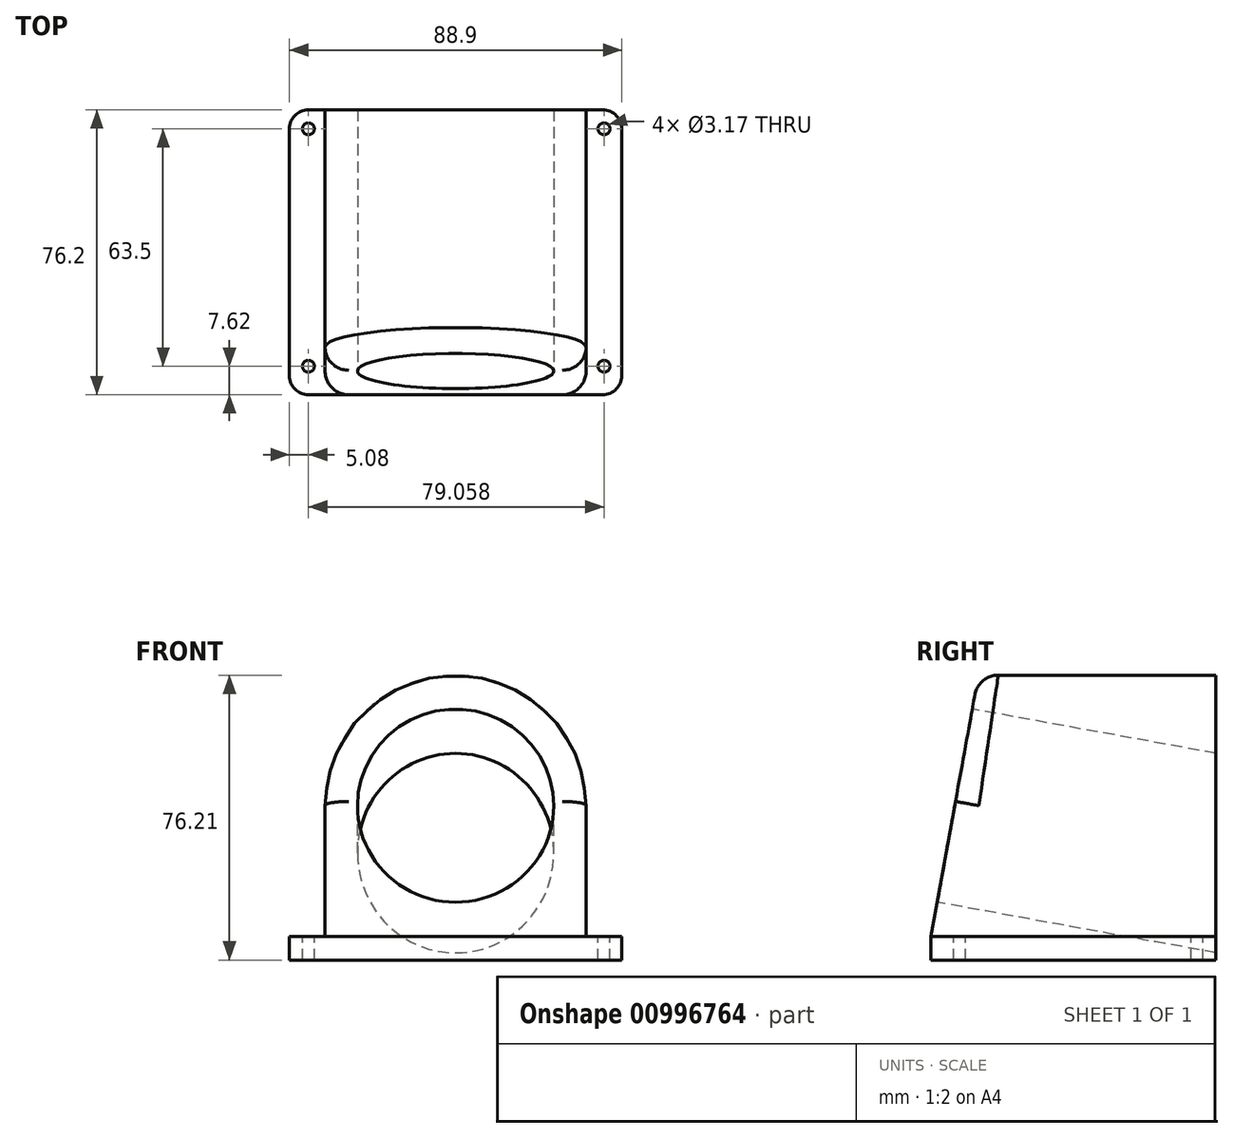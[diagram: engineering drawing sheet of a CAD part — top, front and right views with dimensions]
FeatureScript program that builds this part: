
annotation { "Feature Type Name" : "Feature", "Feature Type Description" : "" }
export const myFeature = defineFeature(function(context is Context, id is Id, definition is map)
    precondition{}
    {
        {
            var Q0;
            Q0=qCreatedBy(makeId("Front.planeOp"),FACE);
            var sketch = newSketch(context, id + "F0", { "sketchPlane" : qUnion([Q0])});
            skLineSegment(sketch, "E0.top", {"start": v(34.92, -34.93) * mm, "end": v(-34.93, -34.93) * mm});
            skLineSegment(sketch, "E0.left", {"start": v(34.92, 0) * mm, "end": v(34.92, -34.93) * mm});
            skLineSegment(sketch, "E0.right", {"start": v(-34.93, 0) * mm, "end": v(-34.93, -34.93) * mm});
            skPoint(sketch, "E0.middle", {"position": v(0, 0) * mm});
            skArc(sketch, "E1", {"start": v(34.93, 0) * mm, "mid": v(0, 34.93) * mm, "end": v(-34.93, 0) * mm});
            skPoint(sketch, "E2.orphan", {"position": v(-34.92, 34.92) * mm});
            skPoint(sketch, "E3.orphan", {"position": v(34.93, 34.93) * mm});
            skSolve(sketch);
        }
        {
            var Q0;
            Q0=makeQuery(id+"F0.imprint","IMPRINT",FACE,{"disambiguationData":[TD([[makeQuery(id+"F0.imprint","IMPRINT",EDGE,{"derivedFrom":sQuery(id+"F0.wireOp",EDGE,"E0.top")}),-1.0]])]});
            extrude(context, id + "F1", {"entities" : qUnion([Q0]), "depth" : 76.2 * mm, "offsetDistance" : 25.4 * mm});
        }
        {
            var Q0;
            Q0=makeQuery(id+"F1.opExtrude","SWEPT_FACE",FACE,{"disambiguationData":[OSD([sQuery(id+"F0.wireOp",EDGE,"E0.left")])]});
            var sketch = newSketch(context, id + "F2", { "sketchPlane" : qUnion([Q0])});
            skLineSegment(sketch, "E4", {"start": v(-76.2, -34.92) * mm, "end": v(-76.2, 35.13) * mm});
            skLineSegment(sketch, "E5", {"start": v(-76.2, 35.13) * mm, "end": v(-63.5, 35.13) * mm});
            skLineSegment(sketch, "E6", {"start": v(-63.5, 35.13) * mm, "end": v(-76.2, -34.93) * mm});
            skSolve(sketch);
        }
        {
            var Q0;
            Q0 = qSketchRegion(id + "F2", true);
            extrude(context, id + "F3", {"entities" : qUnion([Q0]), "operationType" : NewBodyOperationType.REMOVE, "endBound" : BoundingType.THROUGH_ALL, "oppositeDirection" : true, "depth" : 25.4 * mm, "offsetDistance" : 25.4 * mm});
        }
        {
            var Q0;
            Q0=makeQuery(id+"F3.boolean.opBoolean","COPY",FACE,{"derivedFrom":makeQuery(id+"F3.opExtrude","SWEPT_FACE",FACE,{"disambiguationData":[OSD([sQuery(id+"F2.wireOp",EDGE,"E6")])]})});
            var sketch = newSketch(context, id + "F4", { "sketchPlane" : qUnion([Q0])});
            skCircle(sketch, "E7", {"center": v(0, -12.46) * mm, "radius": 26.25 * mm});
            skSolve(sketch);
        }
        {
            var Q0;
            Q0=makeQuery(id+"F1.opExtrude","CAP_FACE",FACE,{"disambiguationData":[OSD([sQuery(id+"F0.wireOp",EDGE,"E0.top"),sQuery(id+"F0.wireOp",EDGE,"E0.left"),sQuery(id+"F0.wireOp",EDGE,"E0.right"),sQuery(id+"F0.wireOp",EDGE,"E1")])],"isStart":true});
            var sketch = newSketch(context, id + "F5", { "sketchPlane" : qUnion([Q0])});
            skLineSegment(sketch, "E8.bottom", {"start": v(-44.45, -34.93) * mm, "end": v(44.45, -34.93) * mm});
            skLineSegment(sketch, "E8.top", {"start": v(-44.45, -41.28) * mm, "end": v(44.45, -41.28) * mm});
            skLineSegment(sketch, "E8.left", {"start": v(-44.45, -34.93) * mm, "end": v(-44.45, -41.28) * mm});
            skLineSegment(sketch, "E8.right", {"start": v(44.45, -34.93) * mm, "end": v(44.45, -41.28) * mm});
            skSolve(sketch);
        }
        {
            var Q0;
            Q0=makeQuery(id+"F5.imprint","IMPRINT",FACE,{"disambiguationData":[TD([[makeQuery(id+"F5.imprint","IMPRINT",EDGE,{"derivedFrom":sQuery(id+"F5.wireOp",EDGE,"E8.top")}),1.0]])]});
            extrude(context, id + "F6", {"entities" : qUnion([Q0]), "operationType" : NewBodyOperationType.ADD, "oppositeDirection" : true, "depth" : 76.2 * mm, "offsetDistance" : 25.4 * mm});
        }
        {
            var Q0;
            Q0 = qSketchRegion(id + "F4", true);
            extrude(context, id + "F7", {"entities" : qUnion([Q0]), "operationType" : NewBodyOperationType.REMOVE, "endBound" : BoundingType.THROUGH_ALL, "oppositeDirection" : true, "depth" : 25.4 * mm, "offsetDistance" : 25.4 * mm});
        }
        {
            var Q0;
            Q0=makeQuery(id+"F3.boolean.opBoolean","INTERSECT",EDGE,{"derivedFrom":[makeQuery(id+"F1.opExtrude","SWEPT_FACE",FACE,{"disambiguationData":[OSD([sQuery(id+"F0.wireOp",EDGE,"E1")])]}),makeQuery(id+"F3.opExtrude","SWEPT_FACE",FACE,{"disambiguationData":[OSD([sQuery(id+"F2.wireOp",EDGE,"E6")])]})]});
            fillet(context, id + "F8", {"entities" : qUnion([Q0]), "radius" : 6.35 * mm, "tangentPropagation" : true, "allowEdgeOverflow" : false});
        }
        {
            var Q0;
            Q0=makeQuery(id+"F6.opExtrude","CAP_EDGE",EDGE,{"disambiguationData":[OSD([sQuery(id+"F5.wireOp",EDGE,"E8.right")])],"isStart":false});
            var Q1;
            Q1=makeQuery(id+"F6.opExtrude","CAP_EDGE",EDGE,{"disambiguationData":[OSD([sQuery(id+"F5.wireOp",EDGE,"E8.right")])],"isStart":true});
            var Q2;
            Q2=makeQuery(id+"F6.opExtrude","CAP_EDGE",EDGE,{"disambiguationData":[OSD([sQuery(id+"F5.wireOp",EDGE,"E8.left")])],"isStart":false});
            var Q3;
            Q3=makeQuery(id+"F6.opExtrude","CAP_EDGE",EDGE,{"disambiguationData":[OSD([sQuery(id+"F5.wireOp",EDGE,"E8.left")])],"isStart":true});
            fillet(context, id + "F9", {"entities" : qUnion([Q0, Q1, Q2, Q3]), "radius" : 5.08 * mm, "tangentPropagation" : true, "allowEdgeOverflow" : false});
        }
        {
            var Q0;
            {var subQ3=sQuery(id+"F5.wireOp",EDGE,"E8.bottom");var subQ4=sQuery(id+"F0.wireOp",EDGE,"E0.right");Q0=makeQuery(id+"F6.boolean.opBoolean","SPLIT",FACE,{"disambiguationData":[TD([makeQuery(id+"F1.opExtrude","SWEPT_FACE",FACE,{"disambiguationData":[OSD([subQ4])]})])],"derivedFrom":makeQuery(id+"F6.opExtrude","SWEPT_FACE",FACE,{"disambiguationData":[OSD([subQ3])]})});}
            var sketch = newSketch(context, id + "F10", { "sketchPlane" : qUnion([Q0])});
            skCircle(sketch, "E9", {"center": v(-39.37, -5.08) * mm, "radius": 1.59 * mm});
            skCircle(sketch, "E10", {"center": v(-39.37, -68.58) * mm, "radius": 1.59 * mm});
            skCircle(sketch, "E11", {"center": v(39.69, -68.58) * mm, "radius": 1.59 * mm});
            skCircle(sketch, "E12", {"center": v(39.69, -5.08) * mm, "radius": 1.59 * mm});
            skSolve(sketch);
        }
        {
            var Q0;
            Q0=makeQuery(id+"F10.imprint","IMPRINT",FACE,{"disambiguationData":[TD([[makeQuery(id+"F10.imprint","IMPRINT",EDGE,{"derivedFrom":sQuery(id+"F10.wireOp",EDGE,"E9")}),1.0]])]});
            var Q1;
            Q1=makeQuery(id+"F10.imprint","IMPRINT",FACE,{"disambiguationData":[TD([[makeQuery(id+"F10.imprint","IMPRINT",EDGE,{"derivedFrom":sQuery(id+"F10.wireOp",EDGE,"E10")}),1.0]])]});
            var Q2;
            Q2=makeQuery(id+"F10.imprint","IMPRINT",FACE,{"disambiguationData":[TD([[makeQuery(id+"F10.imprint","IMPRINT",EDGE,{"derivedFrom":sQuery(id+"F10.wireOp",EDGE,"E11")}),1.0]])]});
            var Q3;
            Q3=makeQuery(id+"F10.imprint","IMPRINT",FACE,{"disambiguationData":[TD([[makeQuery(id+"F10.imprint","IMPRINT",EDGE,{"derivedFrom":sQuery(id+"F10.wireOp",EDGE,"E12")}),1.0]])]});
            extrude(context, id + "F11", {"entities" : qUnion([Q0, Q1, Q2, Q3]), "operationType" : NewBodyOperationType.REMOVE, "oppositeDirection" : true, "depth" : 25.4 * mm, "offsetDistance" : 25.4 * mm});
        }
    });
